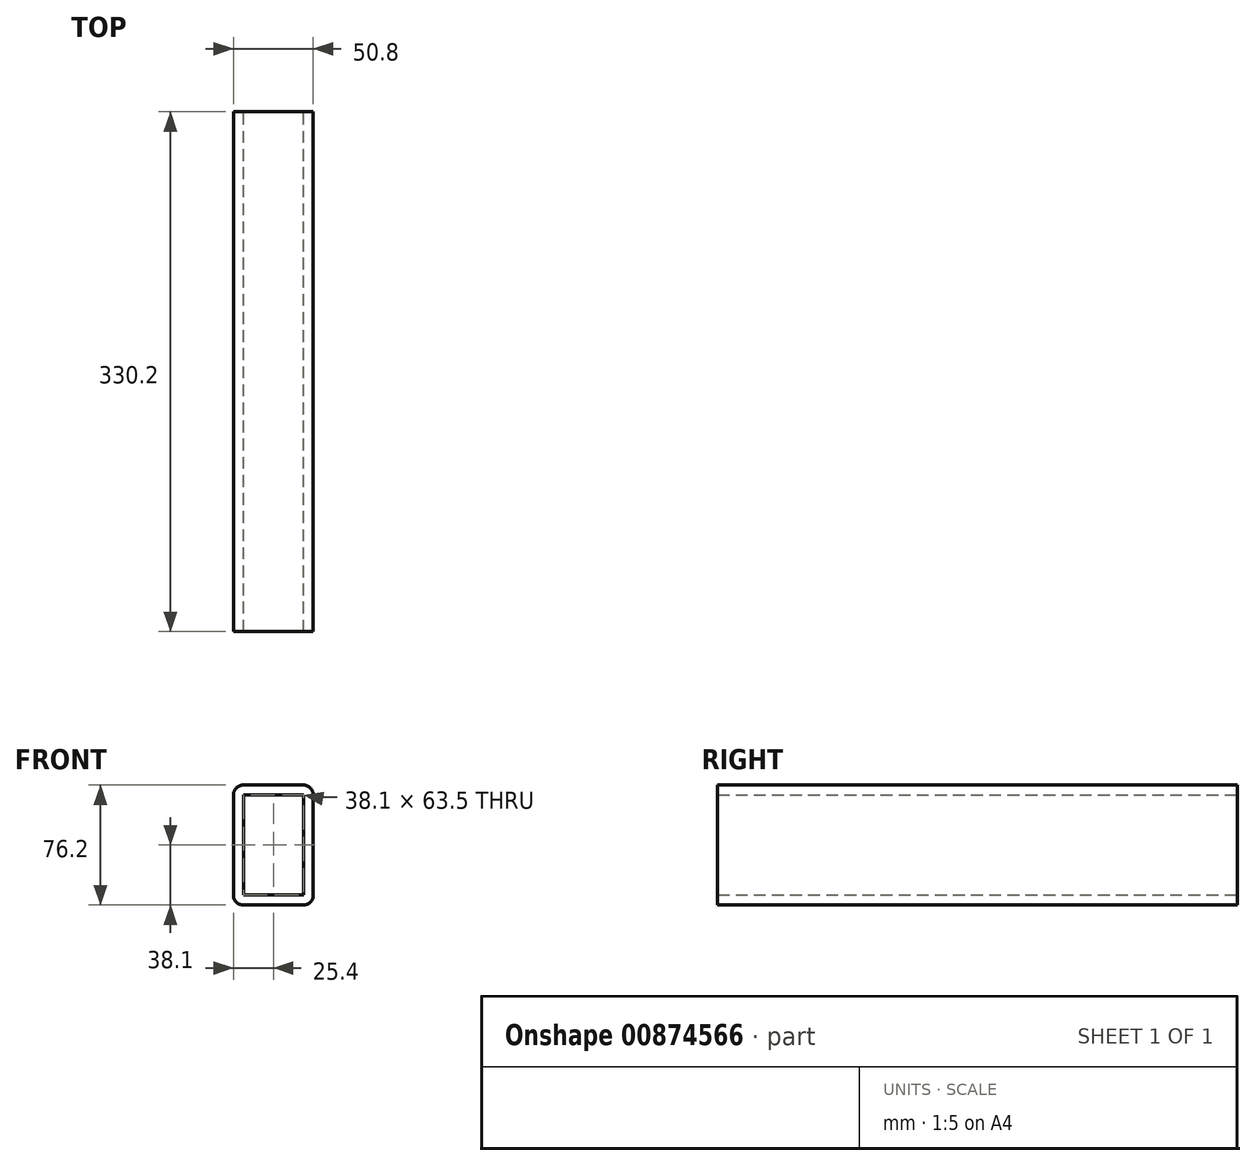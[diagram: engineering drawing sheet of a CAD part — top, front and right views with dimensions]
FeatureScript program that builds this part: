
annotation { "Feature Type Name" : "Feature", "Feature Type Description" : "" }
export const myFeature = defineFeature(function(context is Context, id is Id, definition is map)
    precondition{}
    {
        {
            var Q0;
            Q0=qCreatedBy(makeId("Front.planeOp"),FACE);
            var sketch = newSketch(context, id + "F0", { "sketchPlane" : qUnion([Q0])});
            skLineSegment(sketch, "E0.bottom", {"start": v(-19.05, 38.1) * mm, "end": v(19.05, 38.1) * mm});
            skLineSegment(sketch, "E0.top", {"start": v(-19.05, -38.1) * mm, "end": v(19.05, -38.1) * mm});
            skLineSegment(sketch, "E0.left", {"start": v(-25.4, 31.75) * mm, "end": v(-25.4, -31.75) * mm});
            skLineSegment(sketch, "E0.right", {"start": v(25.4, 31.75) * mm, "end": v(25.4, -31.75) * mm});
            skPoint(sketch, "E0.middle", {"position": v(0, 0) * mm});
            skLineSegment(sketch, "E1.bottom", {"start": v(-19.05, 31.75) * mm, "end": v(19.05, 31.75) * mm});
            skLineSegment(sketch, "E1.top", {"start": v(-19.05, -31.75) * mm, "end": v(19.05, -31.75) * mm});
            skLineSegment(sketch, "E1.left", {"start": v(-19.05, 31.75) * mm, "end": v(-19.05, -31.75) * mm});
            skLineSegment(sketch, "E1.right", {"start": v(19.05, 31.75) * mm, "end": v(19.05, -31.75) * mm});
            skPoint(sketch, "E2.visualSharp", {"position": v(-25.4, 38.1) * mm});
            skArc(sketch, "E2.filletArc", {"start": v(-19.05, 38.1) * mm, "mid": v(-23.54, 36.24) * mm, "end": v(-25.4, 31.75) * mm});
            skPoint(sketch, "E3.visualSharp", {"position": v(25.4, 38.1) * mm});
            skArc(sketch, "E3.filletArc", {"start": v(25.4, 31.75) * mm, "mid": v(23.54, 36.24) * mm, "end": v(19.05, 38.1) * mm});
            skPoint(sketch, "E4.visualSharp", {"position": v(25.4, -38.1) * mm});
            skArc(sketch, "E4.filletArc", {"start": v(19.05, -38.1) * mm, "mid": v(23.54, -36.24) * mm, "end": v(25.4, -31.75) * mm});
            skPoint(sketch, "E5.visualSharp", {"position": v(-25.4, -38.1) * mm});
            skArc(sketch, "E5.filletArc", {"start": v(-25.4, -31.75) * mm, "mid": v(-23.54, -36.24) * mm, "end": v(-19.05, -38.1) * mm});
            skSolve(sketch);
        }
        {
            var Q0;
            Q0=makeQuery(id+"F0.imprint","IMPRINT",FACE,{"disambiguationData":[TD([[makeQuery(id+"F0.imprint","IMPRINT",EDGE,{"derivedFrom":sQuery(id+"F0.wireOp",EDGE,"E0.bottom")}),-1.0]])]});
            extrude(context, id + "F1", {"entities" : qUnion([Q0]), "depth" : 330.2 * mm, "offsetDistance" : 25.4 * mm});
        }
    });
